# Revit family: KingswayGroup_Ddblts_QuarterTurnDeadbolt
name_source: partatom
category: Specialty Equipment
units: mm (PartAtom-declared; Revit-internal decimal feet)

## family parameters
Always vertical = No
Cut with Voids When Loaded = No
Part Type = Normal
Room Calculation Point = No
Round Connector Dimension = Use Diameter
Shared = No
Work Plane-Based = Yes

## types (2) — shared parameters
AssetType = Fixed
BIMObjectName = KingswayGroup_Deadbolts_QuarterTurnDeadbolt
Category = Pr_30_36_08_20:Deadbolts
Color = For full range of available finishes and colours, contact Kingsway Group
DeadboltMaterial = NBS_Concept
DurationUnit = year
Features = A security bolt fitted to half leaf doors to provide a secure alternative to flush bolts. It is operated using the Kingsway Staff Key and has a 15mm throw for maximum security.
Finish = For full range of available finishes and colours, contact Kingsway Group
IfcExportAs = IfcDiscreteAccessoryType
IfcExportType = USERDEFINED
Manufacturer = Kingsway Group
ManufacturerName = Kingsway Group
ManufacturerURL = https://kingswaygroupglobal.com
Material = For full range of available material, contact Kingsway Group
ProductInformation = https://kingswaygroupglobal.com
URL = https://kingswaygroupglobal.com
Uniclass2015Code = Pr_30_36_08_20
Uniclass2015Title = Deadbolts
Uniclass2015Version = Products v1.36
Version = 1
WarrantyDescription = 5-Year Guarantee *For faulty manufacture and not for damage
WarrantyDurationParts = 5
WarrantyDurationUnit = year
zero-valued in all types: Default Elevation, NominalHeight, NominalLength, NominalWidth

## per-type parameters (varying)
| type | Description | KG220 SquareKey | KG221 OvalKey | Model | ModelNumber | ModelReference | Name |
| KG220 QuarterTurnDeadboltSquareKey | KG220 Quarter Turn Deadbolt Square Key | Yes | No | KG220 | KG220 | Quarter Turn Deadbolt Square Key | Deadbolts_QuarterTurnDeadboltSquareKey_KG220_KingswayGroup |
| KG221 QuarterTurnDeadboltOvalKey | KG221 Quarter Turn Deadbolt Oval Key | No | Yes | KG221 | KG221 | Quarter Turn Deadbolt Oval Key | Deadbolts_QuarterTurnDeadboltOvalKey_KG221_KingswayGroup |

## geometry (parser evidence)
native form markers: Sweep x12
no freeform markers — native parametric forms only
